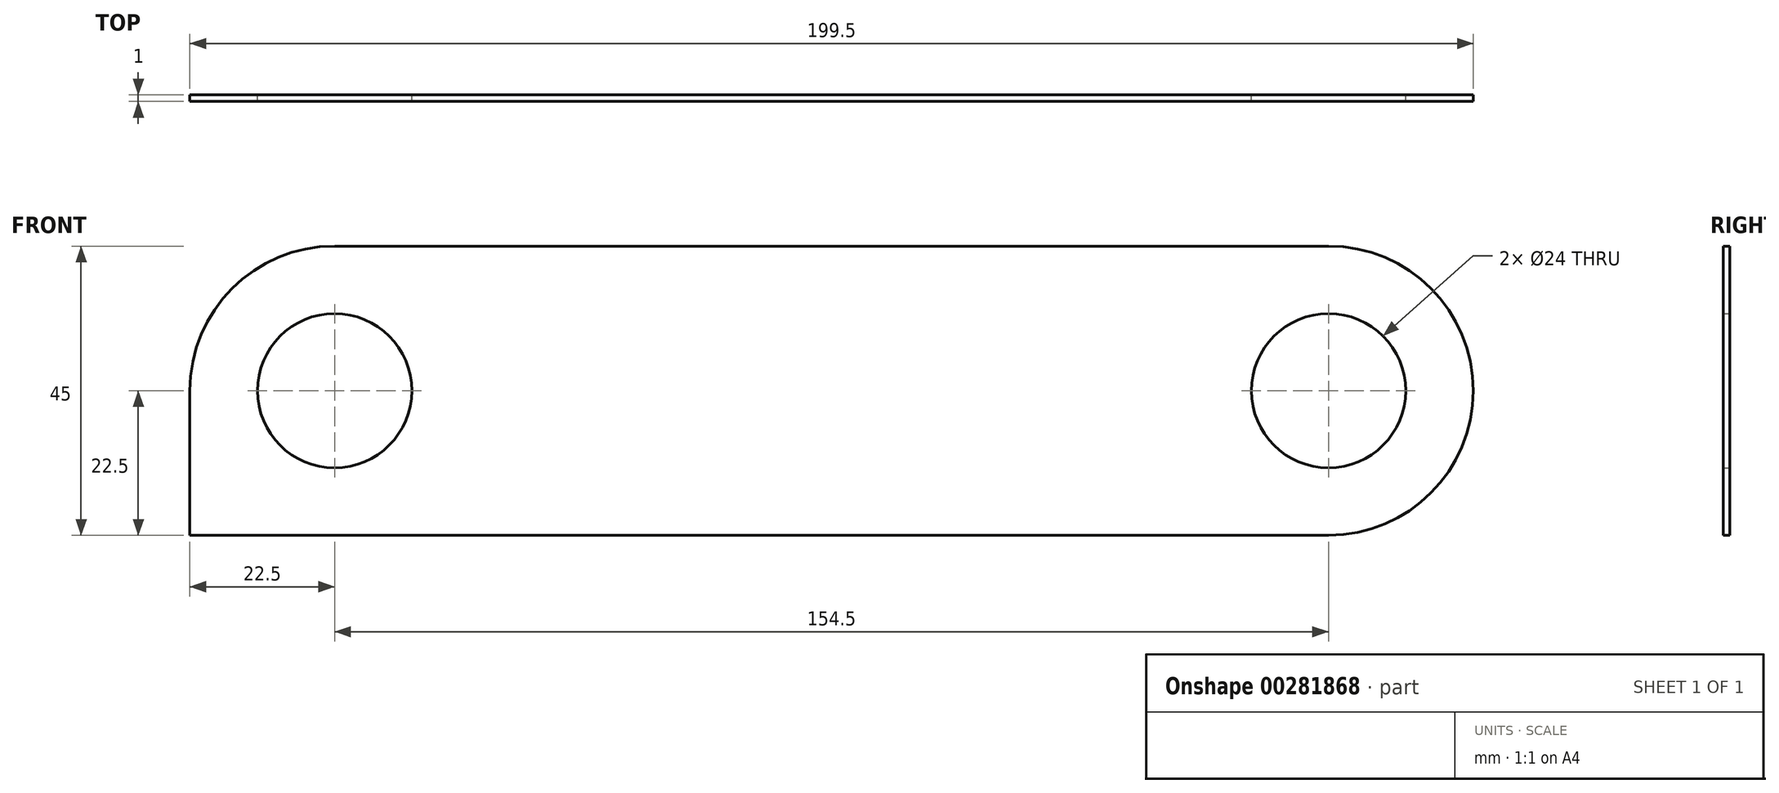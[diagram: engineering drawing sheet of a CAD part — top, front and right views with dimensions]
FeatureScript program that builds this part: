
annotation { "Feature Type Name" : "Feature", "Feature Type Description" : "" }
export const myFeature = defineFeature(function(context is Context, id is Id, definition is map)
    precondition{}
    {
        {
            var Q0;
            Q0=qCreatedBy(makeId("Front.planeOp"),FACE);
            var sketch = newSketch(context, id + "F0", { "sketchPlane" : qUnion([Q0])});
            skLineSegment(sketch, "E0.bottom", {"start": v(0, 22.5) * mm, "end": v(-64.5, 22.5) * mm});
            skLineSegment(sketch, "E0.top", {"start": v(0, -22.5) * mm, "end": v(-64.5, -22.5) * mm});
            skLineSegment(sketch, "E1.bottom", {"start": v(0, 22.5) * mm, "end": v(90, 22.5) * mm});
            skLineSegment(sketch, "E1.top", {"start": v(0, -22.5) * mm, "end": v(90, -22.5) * mm});
            skArc(sketch, "E2", {"start": v(-64.5, 22.5) * mm, "mid": v(-87, 0) * mm, "end": v(-64.5, -22.5) * mm});
            skArc(sketch, "E3", {"start": v(90, -22.5) * mm, "mid": v(112.5, 0) * mm, "end": v(90, 22.5) * mm});
            skCircle(sketch, "E4", {"center": v(-64.5, 0) * mm, "radius": 12 * mm});
            skCircle(sketch, "E5", {"center": v(90, 0) * mm, "radius": 12 * mm});
            skSolve(sketch);
        }
        {
            var Q0;
            Q0 = qSketchRegion(id + "F0", true);
            extrude(context, id + "F1", {"entities" : qUnion([Q0]), "depth" : 1 * mm});
        }
        {
            var Q0;
            Q0=makeQuery(id+"F1.opExtrude","CAP_FACE",FACE,{"disambiguationData":[OSD([sQuery(id+"F0.wireOp",EDGE,"E0.bottom"),sQuery(id+"F0.wireOp",EDGE,"E0.top"),sQuery(id+"F0.wireOp",EDGE,"E1.bottom"),sQuery(id+"F0.wireOp",EDGE,"E1.top"),sQuery(id+"F0.wireOp",EDGE,"E2"),sQuery(id+"F0.wireOp",EDGE,"E3"),sQuery(id+"F0.wireOp",EDGE,"E4"),sQuery(id+"F0.wireOp",EDGE,"E5")])],"isStart":false});
            var sketch = newSketch(context, id + "F2", { "sketchPlane" : qUnion([Q0])});
            skLineSegment(sketch, "E6", {"start": v(-87, 0) * mm, "end": v(-87, -22.5) * mm});
            skLineSegment(sketch, "E7", {"start": v(-87, -22.5) * mm, "end": v(-64.5, -22.5) * mm});
            skLineSegment(sketch, "E8", {"start": v(-64.5, -22.5) * mm, "end": v(-70.42, -18.8) * mm});
            skLineSegment(sketch, "E9", {"start": v(-70.42, -18.8) * mm, "end": v(-80.16, -10.97) * mm});
            skLineSegment(sketch, "E10", {"start": v(-80.16, -10.97) * mm, "end": v(-84.27, -1.93) * mm});
            skLineSegment(sketch, "E11", {"start": v(-84.27, -1.93) * mm, "end": v(-87, 0) * mm});
            skSolve(sketch);
        }
        {
            var Q0;
            Q0 = qSketchRegion(id + "F2", true);
            extrude(context, id + "F3", {"entities" : qUnion([Q0]), "operationType" : NewBodyOperationType.ADD, "oppositeDirection" : true, "depth" : 1 * mm});
        }
    });
